# Revit family: 4466_Addressable External Power Supply
name_source: partatom
category: Fire Alarm Devices
units: mm (PartAtom-declared; Revit-internal decimal feet)

## family parameters
Cut with Voids When Loaded = No
Host = Face
Maintain Annotation Orientation = No
OmniClass Number = 23.85.30.21
OmniClass Title = Environmental Detection/Registration
Part Type = Normal
Room Calculation Point = No
Round Connector Dimension = Use Diameter
Shared = No

## types (1)
- 4466
    24V Outputs = 2 (max. 2A / each)
    Ambient Humidity = Maximum 95 % RH
    Ambient Temperature Operating = -5 to +40 °C
    Ambient Temperature Storage = -20 to +70 °C
    Batteries = Inside the housing (2) 	≤ 7.2 Ah
Outside the housing	≤ 42 Ah
    CPR = 0786-CPR-21627
    Default Elevation = 0 mm  [stored 0 ft]
    Depth (mm) = 95 mm
    Description = Addressable external power supply
    Height (mm) = 298 mm  [stored 0.97769 ft]
    Ingress Protection Rating = IP30
    Manufacturer = Panasonic
    Max_Wire Size = Ø 1.6 mm (2 mm²)
    Min_Wire Size = Ø 0.65 mm (0.33 mm²)
    Model = 4466
    Omniclass Code = 23.85.30.21.11.11.11
    Omniclass Description = Smoke Detectors
    Output Signal = 1  (backwards compatibility only)
    Power Supply = 230 VAC with
protective eart
    Product Material = Metal Housing - Light Grey
    Short Circuit Isolator = Yes (Built-in)
    Terminal Block J3 (Out 0/1) = Ø 2.3 mm (4 mm²)
    Terminal Board Blades For Batteries = 2
    Tested and Approved = EN54-4, EN54-18, EN54-17
    Type Comments = The external power supply 4466 consists of a SMPS (the main power source) and a charger board. It is intended to be used as power supply for external equipment requiring 24 V DC with battery backup.The 4466 shall be connected to the COM loop in order to be monitored by the c.i.e.It is possible to mount and connect to the “2 voltage outputs board” and/or the “com loop repeater 4585” inside the 4466, i.e. in total two expansion boards
    URL = https://www.panasonic-fire-security.com
    Uniclass 2015 Code = Pr_75_80_30_27
    Uniclass 2015 Description = Fire and smoke detector bases
    Uniformat 2010  Code = D7050
    Uniformat 2010 Description = Detection and Alarm
    Vds Approval = G219025
    Version = RVT20
    Weight = 4660g
    Width (mm) = 424 mm  [stored 1.39108 ft]

note: [stored X ft] marks values corroborated as IEEE doubles in the binary element streams (Revit-internal decimal feet)

## geometry (parser evidence)
native form markers: Blend x91, Sweep x2
no freeform markers — native parametric forms only
